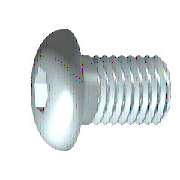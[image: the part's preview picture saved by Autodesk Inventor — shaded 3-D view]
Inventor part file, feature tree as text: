
AUTODESK INVENTOR PART (.ipt)
format: ipt  version: 2024.1 (Build 281209000, 209)  size: 200,704 bytes
history: native  units: mm (DEFAULTED — no unit token found)
features: extrude x1, plane x1, fillet x1
ambient origin geometry x7: Origin, YZ Plane, XY Plane, X Axis, Y Axis, Z Axis, Center Point
bodies: Solid1 (feature_tree), Body (feature_tree)
feature tree (3):
  extrude  "Slot"  Depth=4.5mm
  plane  "Work Plane1"
  fillet  "Fillet2"  Radius=0.306825mm
